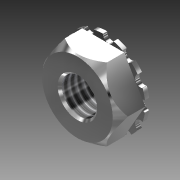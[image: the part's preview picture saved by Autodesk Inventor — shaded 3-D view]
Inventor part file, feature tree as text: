
AUTODESK INVENTOR PART (.ipt)
format: ipt  version: 2011 (Build 150239000, 239)  size: 210,944 bytes
history: native  units: in
note: dims shown in document units (in); Inventor stores cm internally (conversion verified against a paired STEP export)
features: other x2, imported_body x2, thread x1
ambient origin geometry x8: Origin, YZ Plane, XZ Plane, XY Plane, X Axis, Y Axis, Z Axis, Center Point
feature tree (5):
  parser-record x1  (decoder bookkeeping rows leaked as tree rows — omitted from the tree; the rows remain in map.json)
  imported_body  "Base1"
  imported_body  "Base2"
  thread  "Thread1"  [1 undecoded]
  other  "NONE_1"
note: 1 required parameter value undecoded (feature->parameter linkage not recoverable at this tier; creation-order binding heuristic only, values carry confidence <= 0.55)
